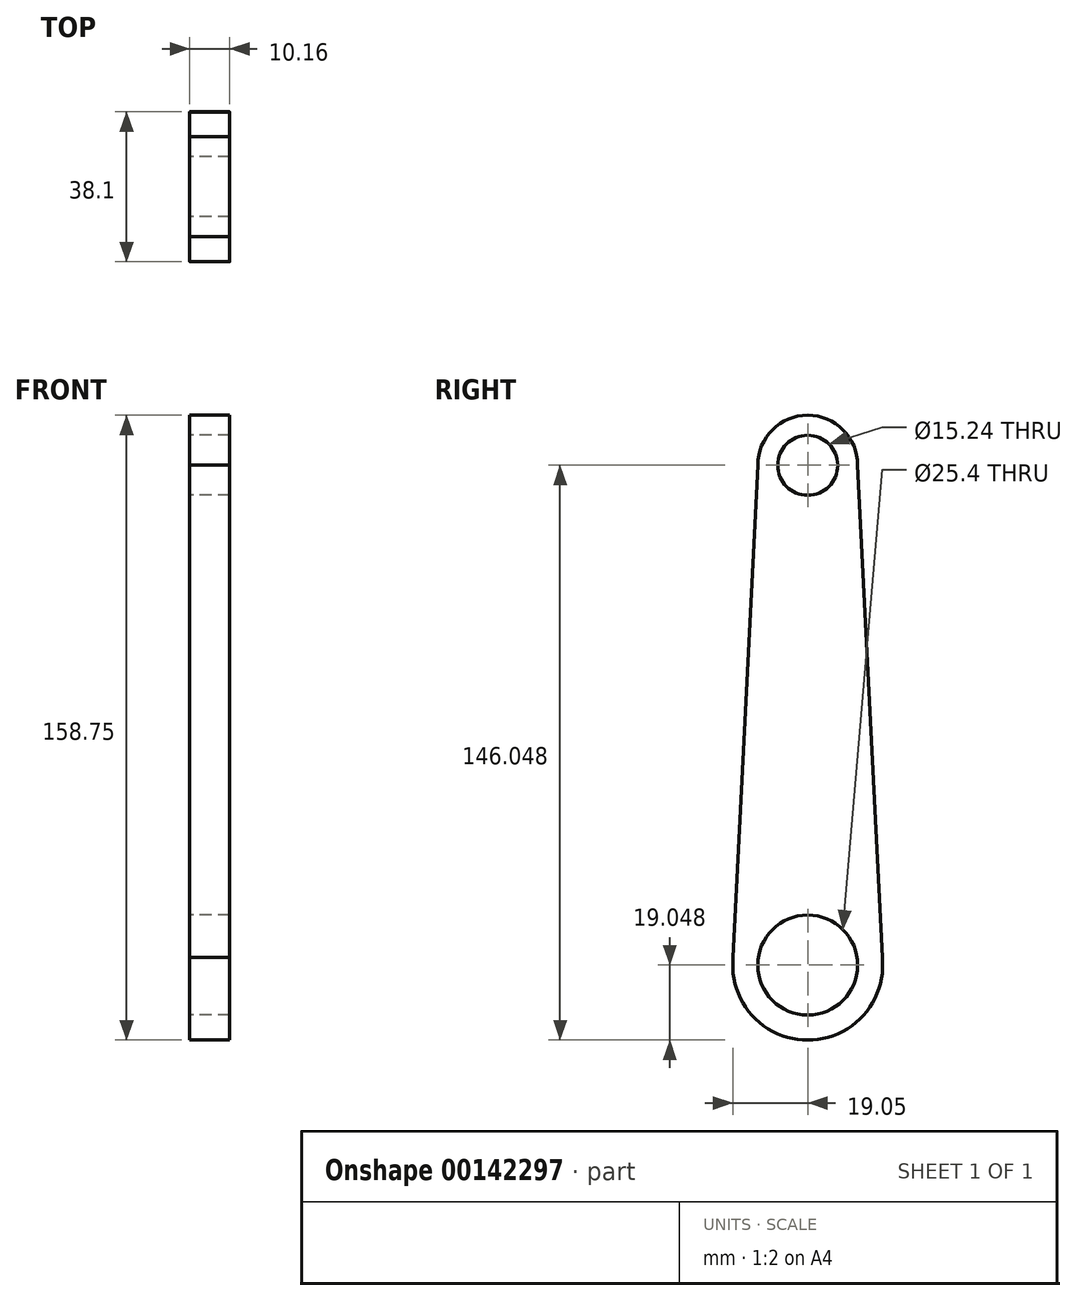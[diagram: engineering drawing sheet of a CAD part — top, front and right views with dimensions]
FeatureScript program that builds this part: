
annotation { "Feature Type Name" : "Feature", "Feature Type Description" : "" }
export const myFeature = defineFeature(function(context is Context, id is Id, definition is map)
    precondition{}
    {
        {
            var Q0;
            Q0=qCreatedBy(makeId("Right.planeOp"),FACE);
            var sketch = newSketch(context, id + "F0", { "sketchPlane" : qUnion([Q0])});
            skCircle(sketch, "E0", {"center": v(0, 80.26) * mm, "radius": 7.62 * mm});
            skCircle(sketch, "E1.0", {"center": v(0, 80.26) * mm, "radius": 12.7 * mm});
            skCircle(sketch, "E2", {"center": v(0, -46.74) * mm, "radius": 12.7 * mm});
            skCircle(sketch, "E3.0", {"center": v(0, -46.74) * mm, "radius": 19.05 * mm});
            skLineSegment(sketch, "E4", {"start": v(-12.7, 80.26) * mm, "end": v(-19.05, -46.74) * mm});
            skLineSegment(sketch, "E5", {"start": v(12.7, 80.26) * mm, "end": v(19.05, -46.74) * mm});
            skSolve(sketch);
        }
        {
            var Q0;
            Q0 = qSketchRegion(id + "F0", true);
            extrude(context, id + "F1", {"entities" : qUnion([Q0]), "depth" : 5.08 * mm, "hasSecondDirection" : true, "secondDirectionOppositeDirection" : true, "secondDirectionDepth" : 5.08 * mm});
        }
    });
